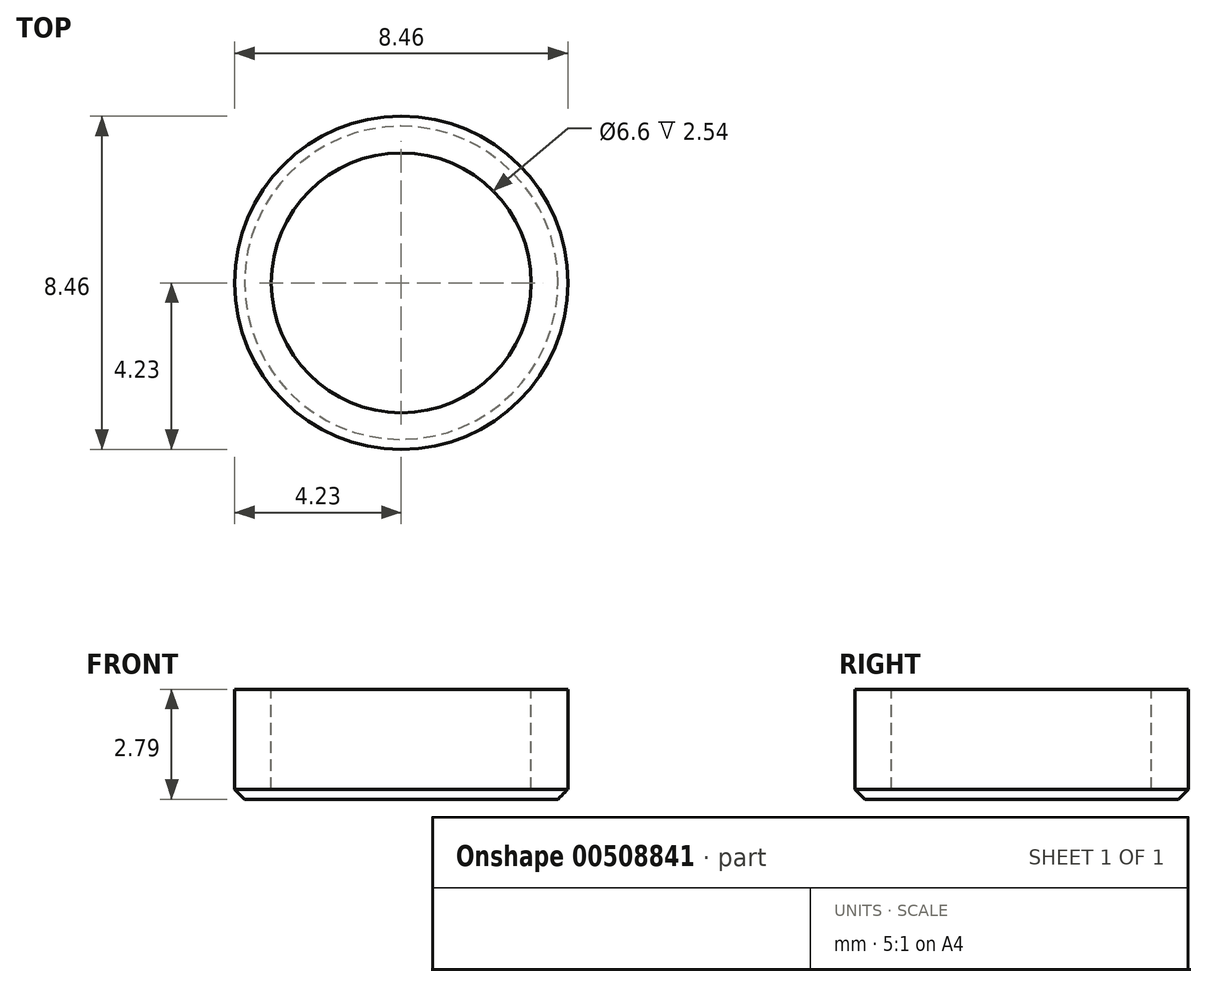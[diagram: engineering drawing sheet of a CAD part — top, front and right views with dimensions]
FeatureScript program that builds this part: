
annotation { "Feature Type Name" : "Feature", "Feature Type Description" : "" }
export const myFeature = defineFeature(function(context is Context, id is Id, definition is map)
    precondition{}
    {
        {
            var Q0;
            Q0=qCreatedBy(makeId("Top.planeOp"),FACE);
            var sketch = newSketch(context, id + "F0", { "sketchPlane" : qUnion([Q0])});
            skCircle(sketch, "E0", {"center": v(0, 0) * mm, "radius": 4.23 * mm});
            skSolve(sketch);
        }
        {
            var Q0;
            Q0 = qSketchRegion(id + "F0", true);
            extrude(context, id + "F1", {"entities" : qUnion([Q0]), "depth" : 2.8 * mm});
        }
        {
            var Q0;
            Q0=makeQuery(id+"F1.opExtrude","CAP_FACE",FACE,{"disambiguationData":[OSD([sQuery(id+"F0.wireOp",EDGE,"E0")])],"isStart":false});
            var sketch = newSketch(context, id + "F2", { "sketchPlane" : qUnion([Q0])});
            skCircle(sketch, "E1", {"center": v(0, 0) * mm, "radius": 3.3 * mm});
            skSolve(sketch);
        }
        {
            var Q0;
            Q0=makeQuery(id+"F2.imprint","IMPRINT",FACE,{"disambiguationData":[TD([[makeQuery(id+"F2.imprint","IMPRINT",EDGE,{"derivedFrom":sQuery(id+"F2.wireOp",EDGE,"E1")}),1.0]])]});
            extrude(context, id + "F3", {"entities" : qUnion([Q0]), "operationType" : NewBodyOperationType.REMOVE, "oppositeDirection" : true, "depth" : 2.54 * mm, "offsetDistance" : 25.4 * mm});
        }
        {
            var Q0;
            Q0=makeQuery(id+"F1.opExtrude","CAP_EDGE",EDGE,{"disambiguationData":[OSD([sQuery(id+"F0.wireOp",EDGE,"E0")])],"isStart":true});
            chamfer(context, id + "F4", {"entities" : qUnion([Q0]), "width" : 0.25 * mm, "tangentPropagation" : true});
        }
    });
